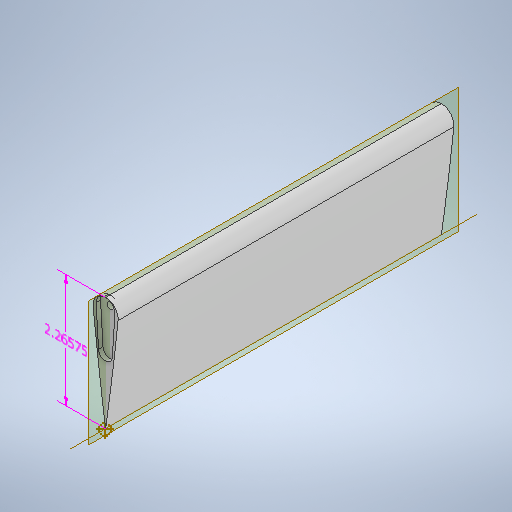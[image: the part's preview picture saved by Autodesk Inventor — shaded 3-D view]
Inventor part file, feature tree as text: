
AUTODESK INVENTOR PART (.ipt)
format: ipt  version: 2025.2 (Build 292293000, 293)  size: 294,912 bytes
history: native  units: in
note: dims shown in document units (in); Inventor stores cm internally (conversion verified against a paired STEP export)
features: other x5, extrude x3, sketch x3, fillet x1, plane x1
ambient origin geometry x8: Origin, YZ Plane, XZ Plane, XY Plane, X Axis, Y Axis, Z Axis, Center Point
bodies: Solid1 (feature_tree)
feature tree (13):
  other  "Elevator"
  other  "Annotations"
  extrude  "Extrusion1"  Depth=0.25in
  fillet  "Fillet1"  Radius=0.0886in
  extrude  "Extrusion2"  Depth=0.187in
  other  "Work Point1"
  plane  "Work Plane1"
  other  "Work Axis1"
  extrude  "Extrusion3"  Depth=2.2657in
  sketch  "Sketch2"  dims[d2=6.693in d3=0.0in d4=0.25in d5=0.0886in d6=0.0in]
  sketch  "Sketch3"  dims[d8=0.125in d10=0.187in]
  sketch  "Sketch5"  dims[d11=6.8898in d12=0.0in d7=2.2657in]
  other  "Linear Dimension 1"
